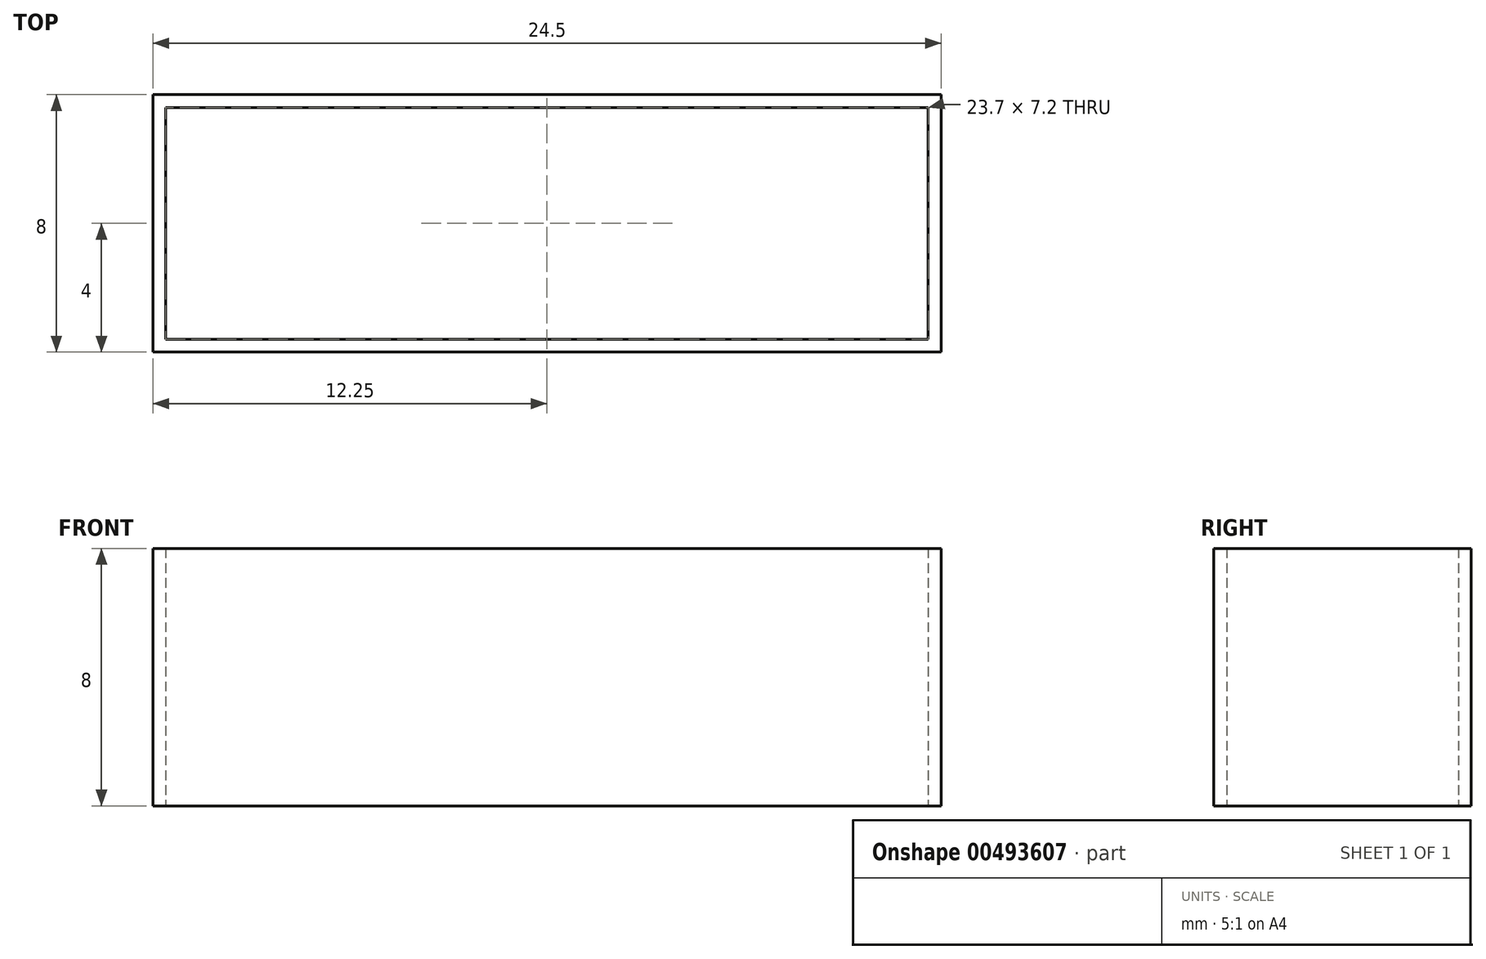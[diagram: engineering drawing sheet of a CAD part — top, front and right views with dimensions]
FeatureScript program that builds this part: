
annotation { "Feature Type Name" : "Feature", "Feature Type Description" : "" }
export const myFeature = defineFeature(function(context is Context, id is Id, definition is map)
    precondition{}
    {
        {
            var Q0;
            Q0=qCreatedBy(makeId("Front.planeOp"),FACE);
            var sketch = newSketch(context, id + "F0", { "sketchPlane" : qUnion([Q0])});
            skLineSegment(sketch, "E0.bottom", {"start": v(-12.25, 4) * mm, "end": v(12.25, 4) * mm});
            skLineSegment(sketch, "E0.top", {"start": v(-12.25, -4) * mm, "end": v(12.25, -4) * mm});
            skLineSegment(sketch, "E0.left", {"start": v(-12.25, 4) * mm, "end": v(-12.25, -4) * mm});
            skLineSegment(sketch, "E0.right", {"start": v(12.25, 4) * mm, "end": v(12.25, -4) * mm});
            skPoint(sketch, "E0.middle", {"position": v(0, 0) * mm});
            skSolve(sketch);
        }
        {
            var Q0;
            Q0=makeQuery(id+"F0.imprint","IMPRINT",FACE,{"disambiguationData":[TD([[makeQuery(id+"F0.imprint","IMPRINT",EDGE,{"derivedFrom":sQuery(id+"F0.wireOp",EDGE,"E0.bottom")}),-1.0]])]});
            extrude(context, id + "F1", {"entities" : qUnion([Q0]), "endBound" : BoundingType.SYMMETRIC, "depth" : 8 * mm});
        }
        {
            var Q0;
            Q0=makeQuery(id+"F1.opExtrude","SWEPT_FACE",FACE,{"disambiguationData":[OSD([sQuery(id+"F0.wireOp",EDGE,"E0.bottom")])]});
            var Q1;
            Q1=makeQuery(id+"F1.opExtrude","SWEPT_FACE",FACE,{"disambiguationData":[OSD([sQuery(id+"F0.wireOp",EDGE,"E0.top")])]});
            shell(context, id + "F2", {"entities" : qUnion([Q0, Q1]), "thickness" : .4 * mm});
        }
    });
